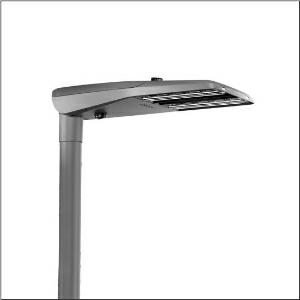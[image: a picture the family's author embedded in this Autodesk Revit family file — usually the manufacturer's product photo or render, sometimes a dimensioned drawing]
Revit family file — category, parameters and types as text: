
# Revit family: streetlight_sl_11_iq_midi___st1_2p1_0_5xc3g51y08me_d530
name_source: partatom
category: Lighting Fixtures
units: mm (PartAtom-declared; Revit-internal decimal feet)

## family parameters
Cut with Voids When Loaded = No
Host = Face
Light Source = No
Part Type = Normal
Room Calculation Point = No
Round Connector Dimension = Use Diameter
Shared = No

## types (1)
- --- (1 x LED, 17750 lm, 122.7 W, 3000K)
    Apparent Load = 123 VA
    CIE Flux Codes = 31 68 95 100 100
    Color Rendering = 70
    Color Temperature = 3000K
    Default Elevation = 1800 mm
    Description = Streetlight SL 11 iQ midi, mast luminaire, primary light control with 3 zone facetted reflector, of plastic, silver coated, highly specular, primary optical cover: cover, of PMMA, transparent, light distribution: ST1.2P1.0, light emission: direct distribution, primary light characteristic: asymmetric, installation type: post-top, side-entry, LED, High Power LED, rated luminous flux: 17.750lm, luminous efficacy: 144lm/W, light colour: 730, colour temperature: 3000K, control: presetting dimming logarithmic, Street-Remote, Auto-Match, Temp-Guard, Lumen-Switch, Night-Set, Smart-Wire, Light-Fading, Desk-Remote (wireless, voltage-free reading and setting of iQ features in the workshop via application-optimized NFC function/RFID function), optimised constant luminous flux control (CLO 2.0), with cable H07RN-F 5x 1.5mm², mains connection: 220..240V, AC, 50/60Hz, connection cable pre-assembled, cable length: 12,5m, start of lifetime: 123W, end of service life: 130W, reduction: 56W, luminaire housing, of diecast aluminium, powder-coated, Siteco® metallic grey (DB 702S), please order mast flange separately, inclination adjustable without tools: 0°, 5°, 10°, 15° (post-top) | 0°, -5°, -10°, -15° (side-entry), sealing non-destructively replaceable, multi-level sealing system, length: 780mm, width: 376mm, height: 118mm, spigot size: 60/76mm (post-top) and 42/60/76mm (side-entry), mast flange for spigot size: 42mm: 5XC10008XM4, 60mm: 5XC10008XM2, 76/60mm: 5XC10108XM1, equipment: Power, Smart Interface below and above, protection rating (complete): IP66, insulation class (complete): insulation class II (safety insulation), certification: CE, ENEC in preparation, impact resistance: IK09, permissible operating ambient temperature for outdoor applications: -25..+50°C, standard-compliant lighting for roads and squares, packaging unit: 1 piece

Light Distribution: ST1.2P1.0
    Height = 118 mm
    Lamp = 1 x LED
    Lamp Light Flux = 17750 lm
    Lamp Power = 122.7 W
    Lamp count = 1
    Length = 780 mm
    Luminous efficacy = 145 lm/W
    Manufacturer = Siteco
    ModVariant = No
    Model = 5XC3G51Y08ME
    Number of Poles = 1
    OnlyDefault = Yes
    Power Factor = 1
    Product Name = Streetlight SL 11 iQ midi | ST1.2P1.0
    Product group = mast luminaire | pylon top
    ProductGroupID = 6100
    Protection Class = Protection class II
    Protection Degree = IP 66
    RLX_Detail_Level = 1
    RlxData = <blob elided: 69449 chars, md5=e9143fd1>
    Socket = socket
    Standby Power = 0 W
    System Light Flux = 17750 lm
    System Power = 123 W
    Type Comments = factory setting: luminous flux: 100 % | dim-lin: 254 | 553 mA
    Type Image = l_1004429.jpg
    URL = http://relux.com
    VarID = @adj_043429
    Voltage = 0 V
    Weight = 0.00 kg
    Width = 376 mm

## geometry (parser evidence)
native form markers: Blend x4, Sweep x10
no freeform markers — native parametric forms only
